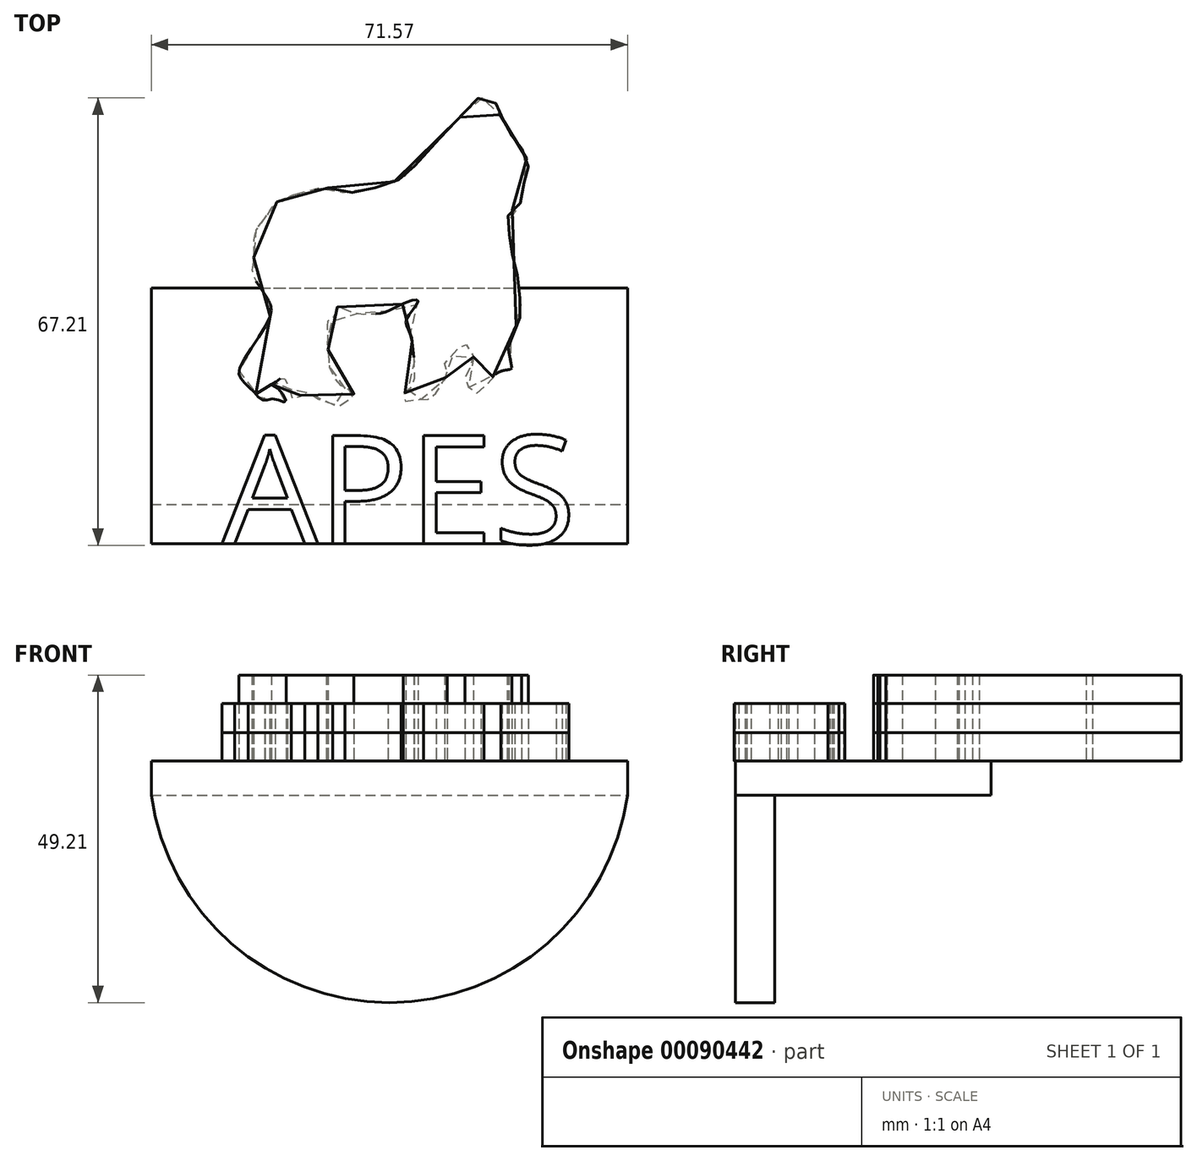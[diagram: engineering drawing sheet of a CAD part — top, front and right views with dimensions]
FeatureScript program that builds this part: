
annotation { "Feature Type Name" : "Feature", "Feature Type Description" : "" }
export const myFeature = defineFeature(function(context is Context, id is Id, definition is map)
    precondition{}
    {
        {
            var Q0;
            Q0=qCreatedBy(makeId("Top.planeOp"),FACE);
            var sketch = newSketch(context, id + "F0", { "sketchPlane" : qUnion([Q0])});
            skText(sketch, "E0", { "text": "APES\n", "fontName": "OpenSans-Regular.ttf"});
            skFitSpline(sketch, "E1", {"points": [v(-44.88, 34.15) * mm, v(-49.4, 26.47) * mm, v(-49.2, 24.7) * mm, v(-47.44, 22.93) * mm, v(-45.86, 21.55) * mm, v(-44.29, 21.75) * mm, v(-42.51, 21.36) * mm, v(-43.9, 23.52) * mm, v(-44.68, 23.91) * mm, v(-43.5, 24.7) * mm, v(-43.1, 25.1) * mm, v(-42.32, 24.3) * mm, v(-41.92, 22.93) * mm, v(-41.14, 21.55) * mm, v(-39.76, 22.73) * mm, v(-37.99, 21.95) * mm, v(-36.41, 21.36) * mm, v(-34.44, 20.77) * mm, v(-32.28, 22.54) * mm, v(-33.66, 23.32) * mm, v(-34.44, 24.11) * mm, v(-35.63, 25.49) * mm, v(-36.02, 27.85) * mm, v(-36.22, 29.43) * mm, v(-36.22, 30.8) * mm, v(-36.22, 32.57) * mm, v(-36.41, 33.56) * mm, v(-35.63, 33.36) * mm, v(-34.84, 35.53) * mm, v(-32.48, 34.74) * mm, v(-30.31, 34.54) * mm, v(-27.75, 34.74) * mm, v(-24.8, 36.12) * mm, v(-22.64, 36.51) * mm, v(-24.19, 34.14) * mm, v(-24.37, 32.84) * mm, v(-23.63, 30.98) * mm, v(-23.44, 29.3) * mm, v(-23.26, 27.82) * mm, v(-23.26, 25.96) * mm, v(-23.44, 23.73) * mm, v(-24.56, 22.8) * mm, v(-24.74, 21.5) * mm, v(-22.52, 21.7) * mm, v(-20.66, 21.88) * mm, v(-19.17, 23.92) * mm, v(-18.24, 25.78) * mm, v(-18.61, 27.26) * mm, v(-17.13, 28.56) * mm, v(-15.83, 30.05) * mm, v(-14.34, 28) * mm, v(-15.46, 25.4) * mm, v(-15.46, 24.3) * mm, v(-13.97, 22.62) * mm, v(-11.55, 24.85) * mm, v(-10.07, 25.96) * mm, v(-8.58, 26.34) * mm, v(-8.95, 26.9) * mm, v(-8.95, 30.05) * mm, v(-7.2, 34.49) * mm, v(-7.2, 36.12) * mm, v(-7.62, 38.56) * mm, v(-7.82, 41) * mm, v(-8.43, 43.04) * mm, v(-8.64, 45.29) * mm, v(-9.04, 46.92) * mm, v(-9.04, 48.95) * mm, v(-9.04, 49.77) * mm, v(-7.41, 51) * mm, v(-6.8, 53.03) * mm, v(-6.6, 55.07) * mm, v(-6.2, 56.09) * mm, v(-6.2, 57.51) * mm, v(-7, 59.14) * mm, v(-7.41, 60.36) * mm, v(-8.64, 61.38) * mm, v(-9.04, 62.8) * mm, v(-10.27, 64.24) * mm, v(-10.67, 65.87) * mm, v(-12.5, 66.89) * mm, v(-13.73, 66.89) * mm, v(-14.75, 65.87) * mm, v(-17.2, 63.22) * mm, v(-22.7, 57.3) * mm, v(-24.12, 55.68) * mm, v(-26.57, 54.25) * mm, v(-29.42, 53.44) * mm, v(-32.07, 52.83) * mm, v(-34.31, 52.83) * mm, v(-36.76, 53.64) * mm, v(-37.57, 53.44) * mm, v(-39, 52.83) * mm, v(-41.24, 52.42) * mm, v(-42.87, 51.8) * mm, v(-44.3, 51) * mm, v(-45.31, 49.36) * mm, v(-46.54, 47.93) * mm, v(-47.35, 45.7) * mm, v(-47.35, 42.64) * mm, v(-47.56, 40.8) * mm, v(-46.13, 38.15) * mm, v(-45.11, 36.52) * mm, v(-44.88, 34.15) * mm]});
            const initialGuessF0  = {"E0": [-0.05211, 0, 1, 0, 0.01637]};
            skSetInitialGuess(sketch, initialGuessF0);
            skSolve(sketch);
        }
        {
            var Q0;
            Q0 = qSketchRegion(id + "F0", true);
            extrude(context, id + "F1", {"entities" : qUnion([Q0]), "depth" : 8.63 * mm});
        }
        {
            var Q0;
            Q0 = qSketchRegion(id + "F0", true);
            var Q1;
            Q1=makeQuery(id+"F1.opExtrude","CAP_FACE",FACE,{"disambiguationData":[OSD([sQuery(id+"F0.wireOp",EDGE,"E1")])],"isStart":false});
            extrude(context, id + "F2", {"entities" : qUnion([Q0, Q1]), "depth" : 4.28 * mm});
        }
        {
            var Q0;
            Q0=qCreatedBy(makeId("Top.planeOp"),FACE);
            var sketch = newSketch(context, id + "F3", { "sketchPlane" : qUnion([Q0])});
            skLineSegment(sketch, "E2.bottom", {"start": v(-62.75, 0) * mm, "end": v(8.82, 0) * mm});
            skLineSegment(sketch, "E2.top", {"start": v(-62.75, 38.43) * mm, "end": v(8.82, 38.43) * mm});
            skLineSegment(sketch, "E2.left", {"start": v(-62.75, 0) * mm, "end": v(-62.75, 38.43) * mm});
            skLineSegment(sketch, "E2.right", {"start": v(8.82, 0) * mm, "end": v(8.82, 38.43) * mm});
            skSolve(sketch);
        }
        {
            var Q0;
            Q0 = qSketchRegion(id + "F3", true);
            extrude(context, id + "F4", {"entities" : qUnion([Q0]), "oppositeDirection" : true, "depth" : 5.12 * mm});
        }
        {
            var Q0;
            Q0=qCreatedBy(makeId("Front.planeOp"),FACE);
            var sketch = newSketch(context, id + "F5", { "sketchPlane" : qUnion([Q0])});
            skPoint(sketch, "E3.0", {"position": v(-62.75, -5.12) * mm});
            skLineSegment(sketch, "E4.0", {"start": v(-62.75, -5.12) * mm, "end": v(8.82, -5.12) * mm});
            skArc(sketch, "E5", {"start": v(-62.75, -5.12) * mm, "mid": v(-26.96, -36.3) * mm, "end": v(8.82, -5.12) * mm});
            skSolve(sketch);
        }
        {
            var Q0;
            Q0 = qSketchRegion(id + "F5", true);
            extrude(context, id + "F6", {"entities" : qUnion([Q0]), "operationType" : NewBodyOperationType.ADD, "oppositeDirection" : true, "depth" : 5.9 * mm});
        }
    });
